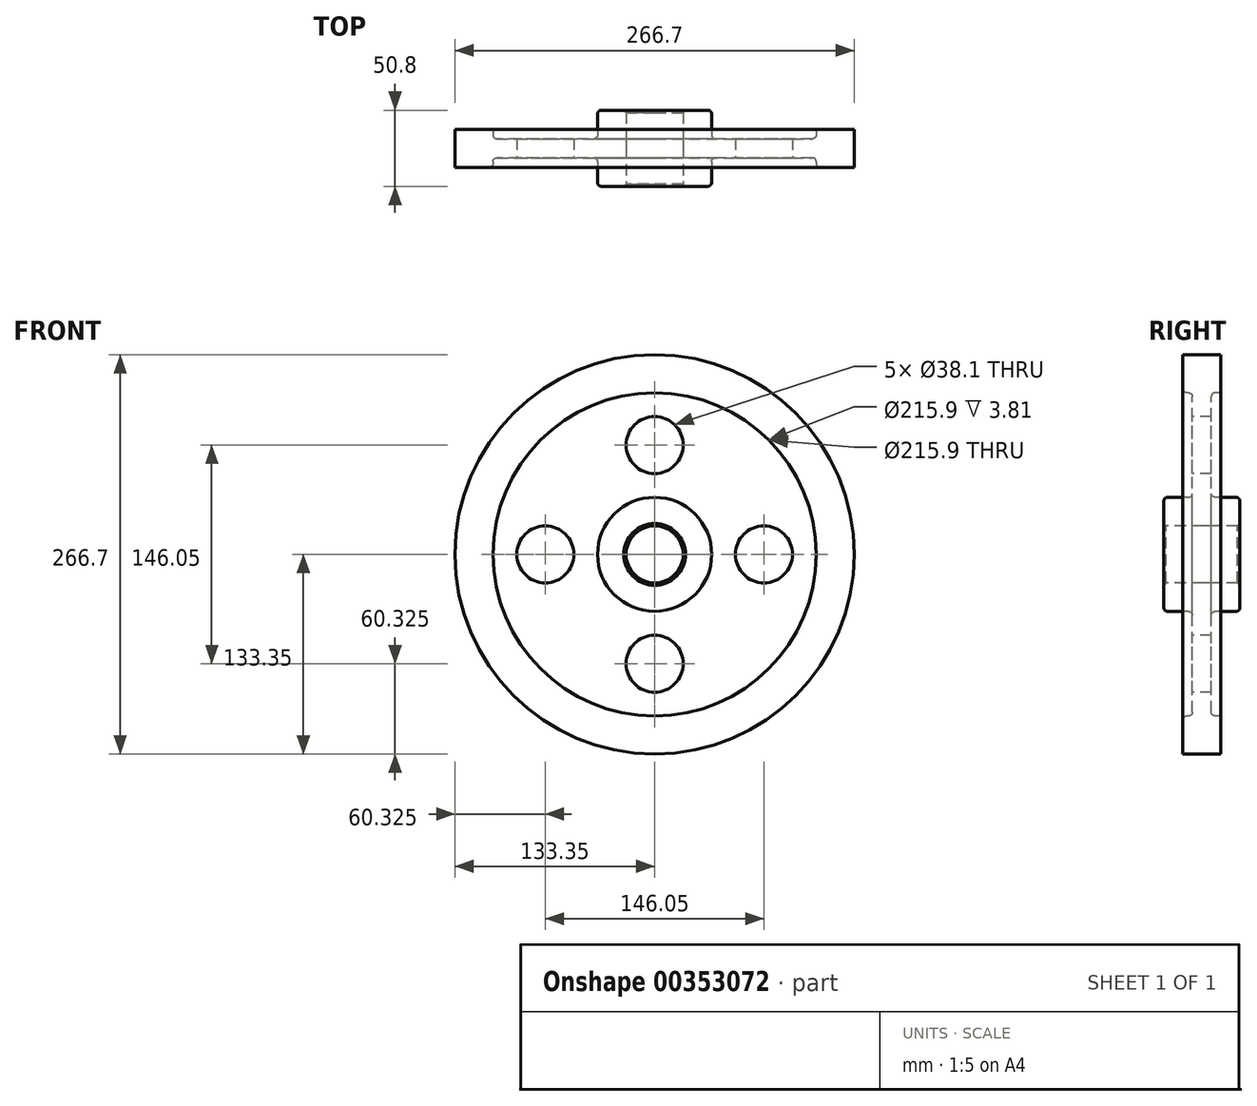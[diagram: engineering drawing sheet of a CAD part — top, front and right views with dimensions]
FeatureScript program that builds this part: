
annotation { "Feature Type Name" : "Feature", "Feature Type Description" : "" }
export const myFeature = defineFeature(function(context is Context, id is Id, definition is map)
    precondition{}
    {
        {
            var Q0;
            Q0=qCreatedBy(makeId("Right.planeOp"),FACE);
            var sketch = newSketch(context, id + "F0", { "sketchPlane" : qUnion([Q0])});
            skLineSegment(sketch, "E0", {"start": v(0, 0) * mm, "end": v(75.93, 0) * mm, "construction": true});
            skLineSegment(sketch, "E1.0", {"start": v(0, 19.05) * mm, "end": v(25.4, 19.05) * mm});
            skLineSegment(sketch, "E2.0", {"start": v(6.35, 38.1) * mm, "end": v(25.4, 38.1) * mm});
            skLineSegment(sketch, "E3.0", {"start": v(6.35, 107.95) * mm, "end": v(12.7, 107.95) * mm});
            skLineSegment(sketch, "E4.0", {"start": v(0, 133.35) * mm, "end": v(12.7, 133.35) * mm});
            skLineSegment(sketch, "E5", {"start": v(0, 0) * mm, "end": v(0, 133.35) * mm, "construction": true});
            skLineSegment(sketch, "E6.0", {"start": v(25.4, 19.05) * mm, "end": v(25.4, 38.1) * mm});
            skLineSegment(sketch, "E7.0", {"start": v(6.35, 38.1) * mm, "end": v(6.35, 107.95) * mm});
            skLineSegment(sketch, "E8.trimOffspring", {"start": v(12.7, 107.95) * mm, "end": v(12.7, 133.35) * mm});
            skLineSegment(sketch, "E9.MirrorCS", {"start": v(-12.7, 107.95) * mm, "end": v(-12.7, 133.35) * mm});
            skLineSegment(sketch, "E10.MirrorCS", {"start": v(0, 133.35) * mm, "end": v(-12.7, 133.35) * mm});
            skLineSegment(sketch, "E11.MirrorCS", {"start": v(-6.35, 38.1) * mm, "end": v(-6.35, 107.95) * mm});
            skLineSegment(sketch, "E12.MirrorCS", {"start": v(-6.35, 38.1) * mm, "end": v(-25.4, 38.1) * mm});
            skLineSegment(sketch, "E13.MirrorCS", {"start": v(0, 19.05) * mm, "end": v(-25.4, 19.05) * mm});
            skLineSegment(sketch, "E14.MirrorCS", {"start": v(-25.4, 19.05) * mm, "end": v(-25.4, 38.1) * mm});
            skLineSegment(sketch, "E15.MirrorCS", {"start": v(-6.35, 107.95) * mm, "end": v(-12.7, 107.95) * mm});
            skSolve(sketch);
        }
        {
            var Q0;
            Q0=makeQuery(id+"F0.imprint","IMPRINT",FACE,{"disambiguationData":[TD([[makeQuery(id+"F0.imprint","IMPRINT",EDGE,{"derivedFrom":sQuery(id+"F0.wireOp",EDGE,"E1.0")}),1.0]])]});
            var Q1;
            Q1=sQuery(id+"F0.wireOp",EDGE,"E0");
            revolve(context, id + "F1", {"entities" : qUnion([Q0]), "axis" : qUnion([Q1]), "revolveType" : RevolveType.FULL});
        }
        {
            var Q0;
            Q0=makeQuery(id+"F1.opRevolve","SWEPT_FACE",FACE,{"disambiguationData":[OSD([sQuery(id+"F0.wireOp",EDGE,"E11.MirrorCS")])]});
            var sketch = newSketch(context, id + "F2", { "sketchPlane" : qUnion([Q0])});
            skLineSegment(sketch, "E16", {"start": v(0, 0) * mm, "end": v(0, 73.03) * mm});
            skCircle(sketch, "E17", {"center": v(0, 73.03) * mm, "radius": 19.05 * mm});
            skCircle(sketch, "E18.1.0", {"center": v(-73.03, 0) * mm, "radius": 19.05 * mm});
            skCircle(sketch, "E18.2.0", {"center": v(0, -73.03) * mm, "radius": 19.05 * mm});
            skCircle(sketch, "E18.3.0", {"center": v(73.03, 0) * mm, "radius": 19.05 * mm});
            skPoint(sketch, "E18.center", {"position": v(0, 0) * mm});
            skSolve(sketch);
        }
        {
            var Q0;
            Q0=makeQuery(id+"F2.imprint","IMPRINT",FACE,{"disambiguationData":[TD([[makeQuery(id+"F2.imprint","IMPRINT",EDGE,{"derivedFrom":sQuery(id+"F2.wireOp",EDGE,"E18.1.0")}),1.0]])]});
            var Q1;
            Q1=makeQuery(id+"F2.imprint","IMPRINT",FACE,{"disambiguationData":[TD([[makeQuery(id+"F2.imprint","IMPRINT",EDGE,{"derivedFrom":sQuery(id+"F2.wireOp",EDGE,"E18.2.0")}),1.0]])]});
            var Q2;
            Q2=makeQuery(id+"F2.imprint","IMPRINT",FACE,{"disambiguationData":[TD([[makeQuery(id+"F2.imprint","IMPRINT",EDGE,{"derivedFrom":sQuery(id+"F2.wireOp",EDGE,"E18.3.0")}),1.0]])]});
            var Q3;
            Q3=makeQuery(id+"F2.imprint","IMPRINT",FACE,{"disambiguationData":[TD([[makeQuery(id+"F2.imprint","IMPRINT",EDGE,{"derivedFrom":sQuery(id+"F2.wireOp",EDGE,"E17")}),1.0]])]});
            extrude(context, id + "F3", {"entities" : qUnion([Q0, Q1, Q2, Q3]), "operationType" : NewBodyOperationType.REMOVE, "oppositeDirection" : true, "depth" : 25.4 * mm});
        }
        {
            var Q0;
            Q0=makeQuery(id+"F1.opRevolve","SWEPT_EDGE",EDGE,{"disambiguationData":[OSD([sQuery(id+"F0.wireOp",EDGE,"E12.MirrorCS"),sQuery(id+"F0.wireOp",EDGE,"E14.MirrorCS")])]});
            var Q1;
            Q1=makeQuery(id+"F1.opRevolve","SWEPT_EDGE",EDGE,{"disambiguationData":[OSD([sQuery(id+"F0.wireOp",EDGE,"E2.0"),sQuery(id+"F0.wireOp",EDGE,"E6.0")])]});
            var Q2;
            {var subQ0=sQuery(id+"F0.wireOp",EDGE,"E11.MirrorCS");Q2=makeQuery(id+"F1edxT1hi52UiFH_1.opFillet","BLEND_EDGE",EDGE,{"blendedFrom":[makeQuery(id+"F1.opRevolve","SWEPT_EDGE",EDGE,{"disambiguationData":[OSD([subQ0,sQuery(id+"F0.wireOp",EDGE,"E12.MirrorCS")])]}),makeQuery(id+"F1.opRevolve","SWEPT_FACE",FACE,{"disambiguationData":[OSD([subQ0])]})],"blendedInto":[makeQuery(id+"F1.opRevolve","SWEPT_FACE",FACE,{"disambiguationData":[OSD([subQ0])]})]});}
            var Q3;
            Q3=makeQuery(id+"F1.opRevolve","SWEPT_EDGE",EDGE,{"disambiguationData":[OSD([sQuery(id+"F0.wireOp",EDGE,"E9.MirrorCS"),sQuery(id+"F0.wireOp",EDGE,"E15.MirrorCS")])]});
            var Q4;
            {var subQ0=sQuery(id+"F0.wireOp",EDGE,"E7.0");Q4=makeQuery(id+"F1edxT1hi52UiFH_1.opFillet","BLEND_EDGE",EDGE,{"blendedFrom":[makeQuery(id+"F1.opRevolve","SWEPT_EDGE",EDGE,{"disambiguationData":[OSD([sQuery(id+"F0.wireOp",EDGE,"E3.0"),subQ0])]}),makeQuery(id+"F1.opRevolve","SWEPT_FACE",FACE,{"disambiguationData":[OSD([subQ0])]})],"blendedInto":[makeQuery(id+"F1.opRevolve","SWEPT_FACE",FACE,{"disambiguationData":[OSD([subQ0])]})]});}
            fillet(context, id + "F4", {"entities" : qUnion([Q0, Q1, Q2, Q3, Q4]), "radius" : 2.54 * mm, "tangentPropagation" : true, "allowEdgeOverflow" : false});
        }
        {
            var Q0;
            Q0=makeQuery(id+"F1.opRevolve","SWEPT_EDGE",EDGE,{"disambiguationData":[OSD([sQuery(id+"F0.wireOp",EDGE,"E13.MirrorCS"),sQuery(id+"F0.wireOp",EDGE,"E14.MirrorCS")])]});
            var Q1;
            Q1=makeQuery(id+"F1.opRevolve","SWEPT_EDGE",EDGE,{"disambiguationData":[OSD([sQuery(id+"F0.wireOp",EDGE,"E1.0"),sQuery(id+"F0.wireOp",EDGE,"E6.0")])]});
            chamfer(context, id + "F5", {"entities" : qUnion([Q0, Q1]), "width" : 1.59 * mm, "tangentPropagation" : true});
        }
        {
            var Q0;
            Q0=makeQuery(id+"F1.opRevolve","SWEPT_EDGE",EDGE,{"disambiguationData":[OSD([sQuery(id+"F0.wireOp",EDGE,"E11.MirrorCS"),sQuery(id+"F0.wireOp",EDGE,"E12.MirrorCS")])]});
            var Q1;
            Q1=makeQuery(id+"F1.opRevolve","SWEPT_EDGE",EDGE,{"disambiguationData":[OSD([sQuery(id+"F0.wireOp",EDGE,"E2.0"),sQuery(id+"F0.wireOp",EDGE,"E7.0")])]});
            var Q2;
            Q2=makeQuery(id+"F1.opRevolve","SWEPT_EDGE",EDGE,{"disambiguationData":[OSD([sQuery(id+"F0.wireOp",EDGE,"E3.0"),sQuery(id+"F0.wireOp",EDGE,"E7.0")])]});
            var Q3;
            Q3=makeQuery(id+"F1.opRevolve","SWEPT_EDGE",EDGE,{"disambiguationData":[OSD([sQuery(id+"F0.wireOp",EDGE,"E11.MirrorCS"),sQuery(id+"F0.wireOp",EDGE,"E15.MirrorCS")])]});
            fillet(context, id + "F6", {"entities" : qUnion([Q0, Q1, Q2, Q3]), "radius" : 2.54 * mm, "tangentPropagation" : true, "allowEdgeOverflow" : false});
        }
    });
